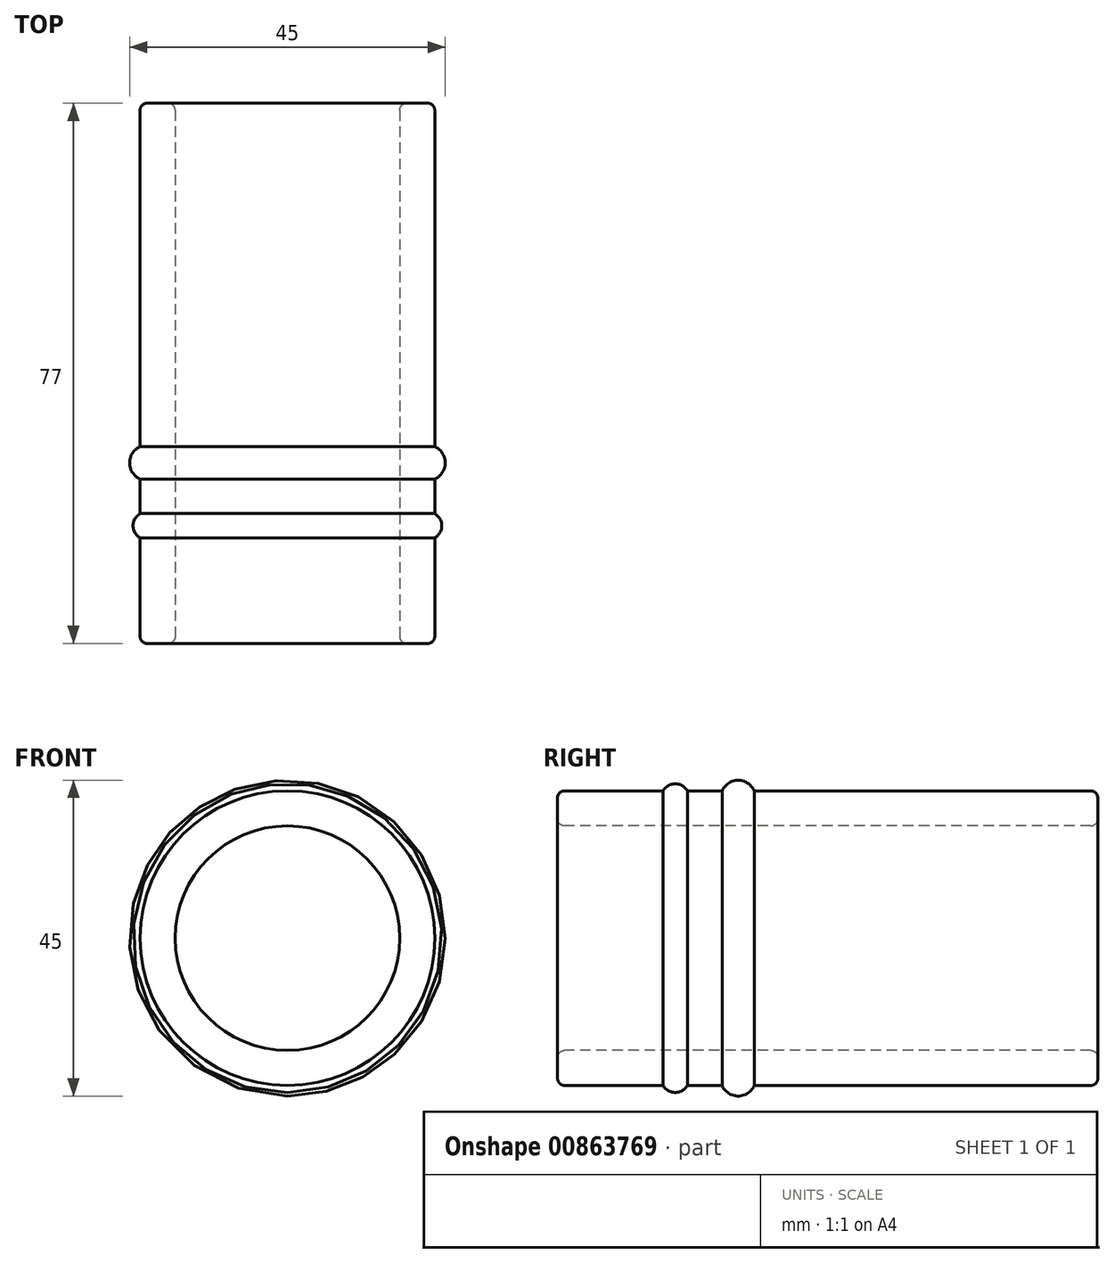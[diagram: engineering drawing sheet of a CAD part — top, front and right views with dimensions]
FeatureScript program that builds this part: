
annotation { "Feature Type Name" : "Feature", "Feature Type Description" : "" }
export const myFeature = defineFeature(function(context is Context, id is Id, definition is map)
    precondition{}
    {
        {
            var Q0;
            Q0=qCreatedBy(makeId("Right.planeOp"),FACE);
            var sketch = newSketch(context, id + "F0", { "sketchPlane" : qUnion([Q0])});
            skLineSegment(sketch, "E0", {"start": v(-27.38, 21) * mm, "end": v(-18.38, 21) * mm});
            skLineSegment(sketch, "E1", {"start": v(48.62, 20) * mm, "end": v(48.62, 17) * mm});
            skLineSegment(sketch, "E2", {"start": v(47.62, 16) * mm, "end": v(-27.38, 16) * mm});
            skLineSegment(sketch, "E3", {"start": v(-28.38, 17) * mm, "end": v(-28.38, 20) * mm});
            skArc(sketch, "E4", {"start": v(-9.87, 21) * mm, "mid": v(-11.6, 22) * mm, "end": v(-13.33, 21) * mm});
            skArc(sketch, "E5", {"start": v(-0.35, 21) * mm, "mid": v(-2.64, 22.5) * mm, "end": v(-4.93, 21) * mm});
            skPoint(sketch, "E6.visualSharp", {"position": v(-28.38, 21) * mm});
            skArc(sketch, "E6.filletArc", {"start": v(-27.38, 21) * mm, "mid": v(-28.08, 20.7) * mm, "end": v(-28.38, 20) * mm});
            skPoint(sketch, "E7.visualSharp", {"position": v(-28.38, 16) * mm});
            skArc(sketch, "E7.filletArc", {"start": v(-28.38, 17) * mm, "mid": v(-28.08, 16.3) * mm, "end": v(-27.38, 16) * mm});
            skPoint(sketch, "E8.visualSharp", {"position": v(48.62, 16) * mm});
            skArc(sketch, "E8.filletArc", {"start": v(47.62, 16) * mm, "mid": v(48.33, 16.3) * mm, "end": v(48.62, 17) * mm});
            skPoint(sketch, "E9.visualSharp", {"position": v(48.62, 21) * mm});
            skArc(sketch, "E9.filletArc", {"start": v(48.62, 20) * mm, "mid": v(48.33, 20.7) * mm, "end": v(47.62, 21) * mm});
            skLineSegment(sketch, "E10.trimOffspring", {"start": v(-18.38, 21) * mm, "end": v(47.62, 21) * mm});
            skLineSegment(sketch, "E11", {"start": v(0, 0) * mm, "end": v(13.85, 0) * mm});
            skSolve(sketch);
        }
        {
            var Q0;
            Q0=makeQuery(id+"F0.imprint","IMPRINT",FACE,{"disambiguationData":[TD([[makeQuery(id+"F0.imprint","IMPRINT",EDGE,{"derivedFrom":sQuery(id+"F0.wireOp",EDGE,"E0")}),-1.0]])]});
            var Q1;
            {var subQ0=sQuery(id+"F0.wireOp",EDGE,"E4");Q1=makeQuery(id+"F0.imprint","IMPRINT",FACE,{"disambiguationData":[TD([[makeQuery(id+"F0.imprint","IMPRINT",EDGE,{"derivedFrom":subQ0}),1.0]])]});}
            var Q2;
            {var subQ0=sQuery(id+"F0.wireOp",EDGE,"E5");Q2=makeQuery(id+"F0.imprint","IMPRINT",FACE,{"disambiguationData":[TD([[makeQuery(id+"F0.imprint","IMPRINT",EDGE,{"derivedFrom":subQ0}),1.0]])]});}
            var Q3;
            Q3=sQuery(id+"F0.wireOp",EDGE,"E11");
            revolve(context, id + "F1", {"surfaceOperationType" : NewSurfaceOperationType.NEW, "entities" : qUnion([Q0, Q1, Q2]), "axis" : qUnion([Q3]), "revolveType" : RevolveType.FULL});
        }
    });
